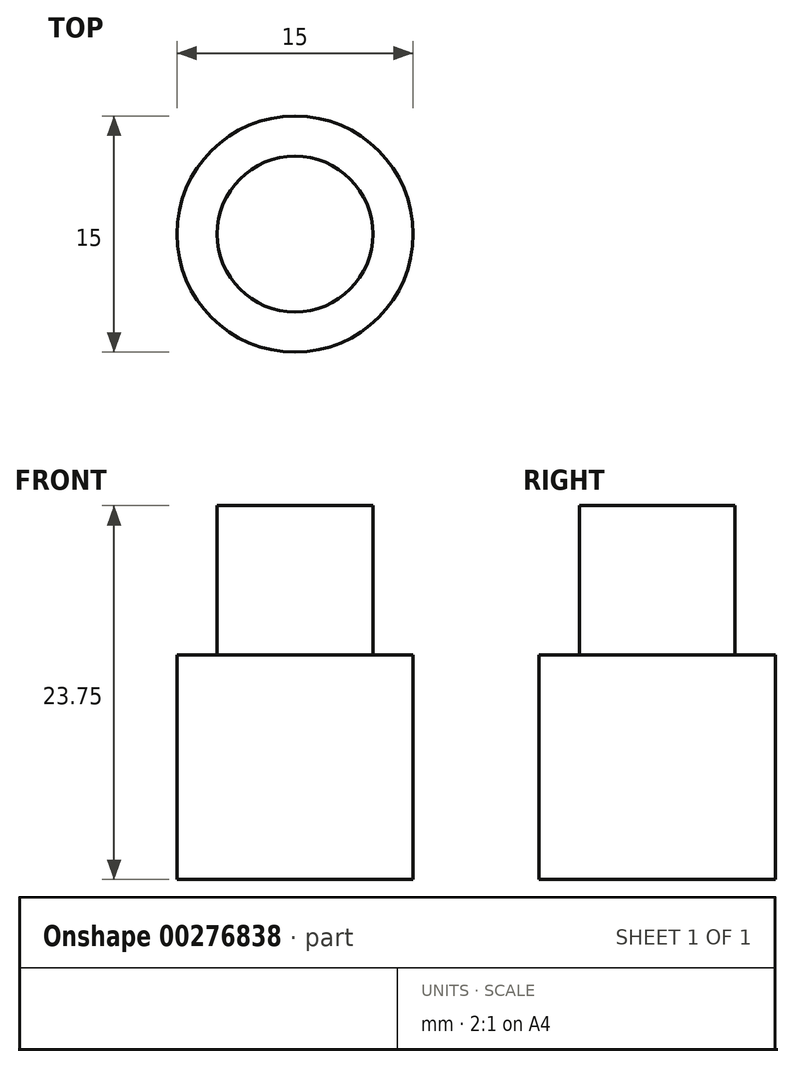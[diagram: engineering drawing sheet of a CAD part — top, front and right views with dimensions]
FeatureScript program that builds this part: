
annotation { "Feature Type Name" : "Feature", "Feature Type Description" : "" }
export const myFeature = defineFeature(function(context is Context, id is Id, definition is map)
    precondition{}
    {
        {
            var Q0;
            Q0=qCreatedBy(makeId("Front.planeOp"),FACE);
            var sketch = newSketch(context, id + "F0", { "sketchPlane" : qUnion([Q0])});
            skLineSegment(sketch, "E0", {"start": v(0, 0) * mm, "end": v(-7.5, 0) * mm});
            skLineSegment(sketch, "E1", {"start": v(-7.5, 0) * mm, "end": v(-7.5, 14.25) * mm});
            skLineSegment(sketch, "E2", {"start": v(-7.5, 14.25) * mm, "end": v(-4.95, 14.25) * mm});
            skLineSegment(sketch, "E3", {"start": v(-4.95, 14.25) * mm, "end": v(-4.95, 23.75) * mm});
            skLineSegment(sketch, "E4", {"start": v(-4.95, 23.75) * mm, "end": v(0, 23.75) * mm});
            skLineSegment(sketch, "E5", {"start": v(0, 23.75) * mm, "end": v(0, 0) * mm});
            skSolve(sketch);
        }
        {
            var Q0;
            Q0=makeQuery(id+"F0.imprint","IMPRINT",FACE,{"disambiguationData":[TD([[makeQuery(id+"F0.imprint","IMPRINT",EDGE,{"derivedFrom":sQuery(id+"F0.wireOp",EDGE,"E0")}),-1.0]])]});
            var Q1;
            Q1=sQuery(id+"F0.wireOp",EDGE,"E5");
            revolve(context, id + "F1", {"entities" : qUnion([Q0]), "axis" : qUnion([Q1]), "revolveType" : RevolveType.FULL});
        }
    });
